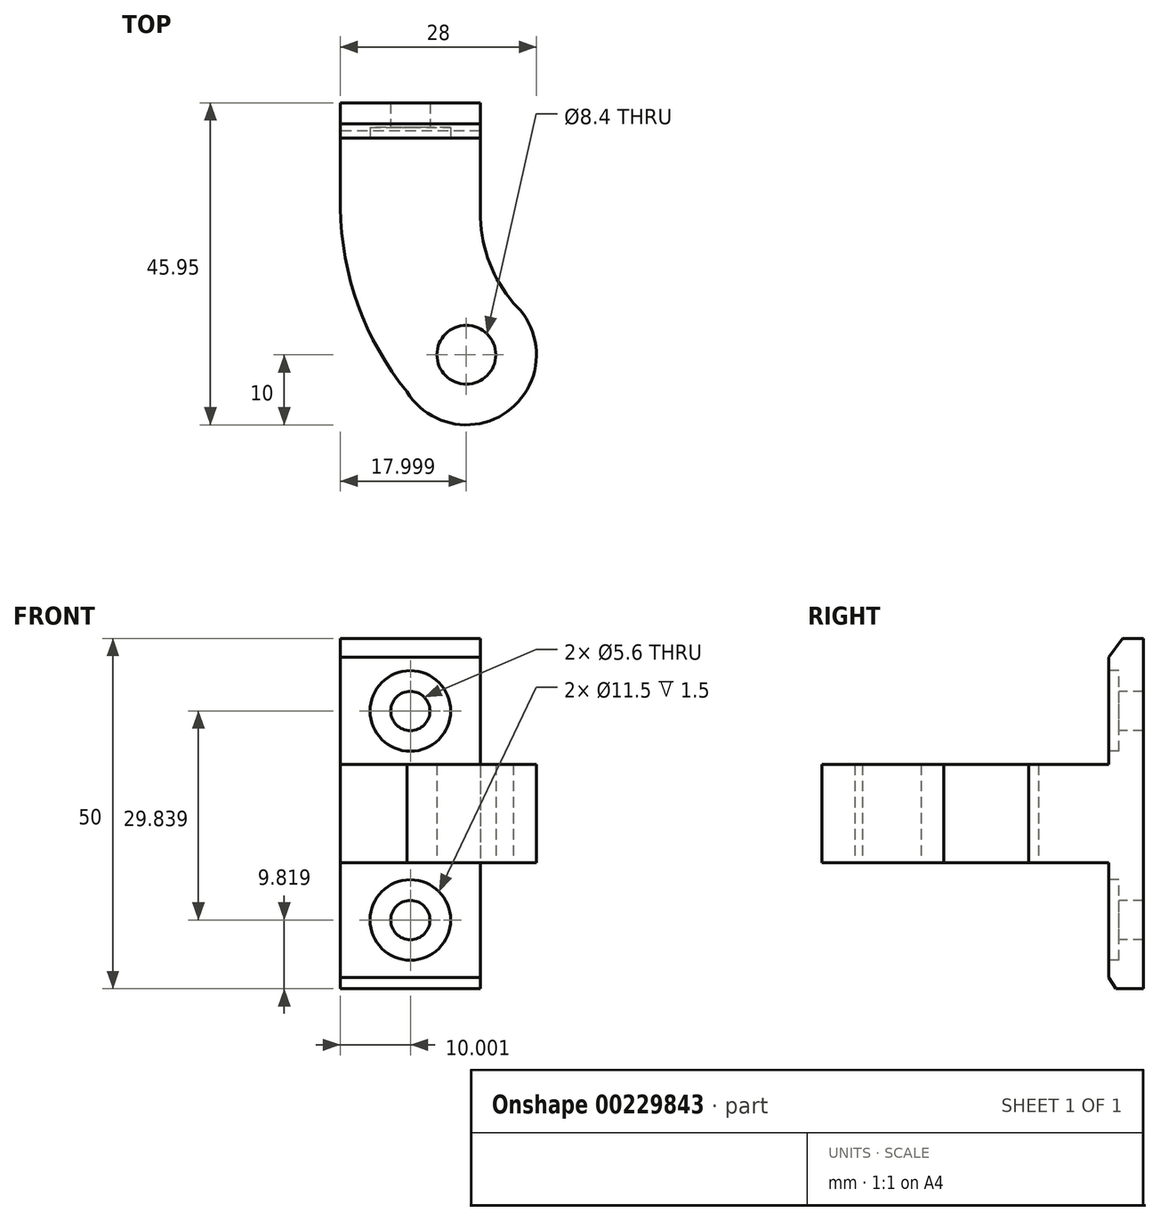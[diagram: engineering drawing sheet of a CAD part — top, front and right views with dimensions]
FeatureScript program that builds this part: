
annotation { "Feature Type Name" : "Feature", "Feature Type Description" : "" }
export const myFeature = defineFeature(function(context is Context, id is Id, definition is map)
    precondition{}
    {
        {
            var Q0;
            Q0=qCreatedBy(makeId("Top.planeOp"),FACE);
            var sketch = newSketch(context, id + "F0", { "sketchPlane" : qUnion([Q0])});
            skLineSegment(sketch, "E0.top", {"start": v(-27.88, 26.05) * mm, "end": v(-5.88, 26.05) * mm});
            skCircle(sketch, "E1", {"center": v(-7.88, -9.9) * mm, "radius": 4.2 * mm});
            skCircle(sketch, "E2", {"center": v(-15.88, 8.05) * mm, "radius": 2.75 * mm, "construction": true});
            skLineSegment(sketch, "E3.bottom", {"start": v(-25.88, 26.05) * mm, "end": v(-5.88, 26.05) * mm});
            skLineSegment(sketch, "E3.top", {"start": v(-19.99, -9.95) * mm, "end": v(-5.88, -9.95) * mm});
            skLineSegment(sketch, "E3.left", {"start": v(-25.88, 26.05) * mm, "end": v(-25.88, 11.06) * mm});
            skLineSegment(sketch, "E3.right", {"start": v(-5.88, 26.05) * mm, "end": v(-5.88, 9.64) * mm});
            skArc(sketch, "E4", {"start": v(-16.38, -15.17) * mm, "mid": v(-1.48, -17.58) * mm, "end": v(-1.16, -2.5) * mm});
            skArc(sketch, "E5", {"start": v(-25.88, 11.06) * mm, "mid": v(-23.32, -2.85) * mm, "end": v(-16.38, -15.17) * mm});
            skArc(sketch, "E6", {"start": v(-5.88, 11.06) * mm, "mid": v(-4.5, 3.04) * mm, "end": v(0, -3.74) * mm});
            skLineSegment(sketch, "E7.trimOffspring", {"start": v(-5.88, -6.2) * mm, "end": v(-5.88, -9.95) * mm});
            skPoint(sketch, "E8.orphan", {"position": v(-25.88, -9.95) * mm});
            skSolve(sketch);
        }
        {
            var Q0;
            Q0 = qSketchRegion(id + "F0", true);
            var Q1;
            {var subQ8=sQuery(id+"F0.wireOp",EDGE,"E3.bottom");Q1=makeQuery(id+"F0.imprint","IMPRINT",FACE,{"disambiguationData":[TD([[makeQuery(id+"F0.imprint","IMPRINT",EDGE,{"derivedFrom":subQ8}),-1.0]])]});}
            extrude(context, id + "F1", {"entities" : qUnion([Q0, Q1]), "depth" : 14 * mm});
        }
        {
            var Q0;
            Q0=makeQuery(id+"F1.opExtrude","CAP_FACE",FACE,{"disambiguationData":[OSD([sQuery(id+"F0.wireOp",EDGE,"E1"),sQuery(id+"F0.wireOp",EDGE,"E3.bottom"),sQuery(id+"F0.wireOp",EDGE,"E3.left"),sQuery(id+"F0.wireOp",EDGE,"E3.right"),sQuery(id+"F0.wireOp",EDGE,"E4"),sQuery(id+"F0.wireOp",EDGE,"E5"),sQuery(id+"F0.wireOp",EDGE,"E6")])],"isStart":false});
            var sketch = newSketch(context, id + "F2", { "sketchPlane" : qUnion([Q0])});
            skLineSegment(sketch, "E9.bottom", {"start": v(-25.88, 26.05) * mm, "end": v(-5.88, 26.05) * mm});
            skLineSegment(sketch, "E9.top", {"start": v(-25.88, 21.05) * mm, "end": v(-5.88, 21.05) * mm});
            skLineSegment(sketch, "E9.left", {"start": v(-25.88, 26.05) * mm, "end": v(-25.88, 21.05) * mm});
            skLineSegment(sketch, "E9.right", {"start": v(-5.88, 26.05) * mm, "end": v(-5.88, 21.05) * mm});
            skLineSegment(sketch, "E10", {"start": v(-25.88, 21.05) * mm, "end": v(-22.88, 21.05) * mm});
            skLineSegment(sketch, "E11", {"start": v(-5.88, 21.05) * mm, "end": v(-8.88, 21.05) * mm});
            skLineSegment(sketch, "E12", {"start": v(-8.88, 21.05) * mm, "end": v(-8.88, 1.78) * mm});
            skLineSegment(sketch, "E13", {"start": v(-22.88, 21.05) * mm, "end": v(-22.88, -4.02) * mm});
            skLineSegment(sketch, "E14", {"start": v(-5.88, 9.64) * mm, "end": v(-25.83, 9.64) * mm});
            skSolve(sketch);
        }
        {
            var Q0;
            Q0=makeQuery(id+"F2.imprint","IMPRINT",FACE,{"disambiguationData":[TD([[makeQuery(id+"F2.imprint","IMPRINT",EDGE,{"derivedFrom":sQuery(id+"F2.wireOp",EDGE,"E9.bottom")}),-1.0]])]});
            var Q1;
            {var subQ0=sQuery(id+"F2.wireOp",EDGE,"E10");Q1=makeQuery(id+"F2.imprint","IMPRINT",FACE,{"disambiguationData":[TD([[makeQuery(id+"F2.imprint","IMPRINT",EDGE,{"derivedFrom":subQ0}),-1.0]])]});}
            var Q2;
            {var subQ4=sQuery(id+"F2.wireOp",EDGE,"E11");Q2=makeQuery(id+"F2.imprint","IMPRINT",FACE,{"disambiguationData":[TD([[makeQuery(id+"F2.imprint","IMPRINT",EDGE,{"derivedFrom":subQ4}),1.0]])]});}
            extrude(context, id + "F3", {"entities" : qUnion([Q0, Q1, Q2]), "operationType" : NewBodyOperationType.ADD, "depth" : 18 * mm});
        }
        {
            var Q0;
            {var subQ0=sQuery(id+"F0.wireOp",EDGE,"E3.right");Q0=makeQuery(id+"F3.boolean.opBoolean","MERGE",FACE,{"derivedFrom":[makeQuery(id+"F1.opExtrude","SWEPT_FACE",FACE,{"disambiguationData":[OSD([subQ0])]}),makeQuery(id+"F3.opExtrude","SWEPT_FACE",FACE,{"disambiguationData":[OSD([subQ0,sQuery(id+"F2.wireOp",EDGE,"E9.right")])]})]});}
            var sketch = newSketch(context, id + "F4", { "sketchPlane" : qUnion([Q0])});
            skLineSegment(sketch, "E15", {"start": v(26.05, 32) * mm, "end": v(23.05, 32) * mm, "construction": true});
            skLineSegment(sketch, "E16", {"start": v(23.05, 32) * mm, "end": v(9.64, 14) * mm});
            skSolve(sketch);
        }
        {
            var Q0;
            {var subQ0=sQuery(id+"F4.wireOp",EDGE,"E16");Q0=makeQuery(id+"F4.imprint","IMPRINT",FACE,{"disambiguationData":[TD([[makeQuery(id+"F4.imprint","IMPRINT",EDGE,{"derivedFrom":subQ0}),-1.0]])]});}
            extrude(context, id + "F5", {"entities" : qUnion([Q0]), "operationType" : NewBodyOperationType.REMOVE, "oppositeDirection" : true, "depth" : 25 * mm});
        }
        {
            var Q0;
            Q0=makeQuery(id+"F3.opExtrude","SWEPT_FACE",FACE,{"disambiguationData":[OSD([sQuery(id+"F2.wireOp",EDGE,"E9.top")])]});
            var sketch = newSketch(context, id + "F6", { "sketchPlane" : qUnion([Q0])});
            skLineSegment(sketch, "E17", {"start": v(-22.88, 21.66) * mm, "end": v(-8.88, 21.66) * mm, "construction": true});
            skCircle(sketch, "E18", {"center": v(-15.88, 21.66) * mm, "radius": 2.8 * mm});
            skSolve(sketch);
        }
        {
            var Q0;
            Q0=makeQuery(id+"F6.imprint","IMPRINT",FACE,{"disambiguationData":[TD([[makeQuery(id+"F6.imprint","IMPRINT",EDGE,{"derivedFrom":sQuery(id+"F6.wireOp",EDGE,"E18")}),1.0]])]});
            extrude(context, id + "F7", {"entities" : qUnion([Q0]), "operationType" : NewBodyOperationType.REMOVE, "oppositeDirection" : true, "depth" : 25 * mm});
        }
        {
            var Q0;
            Q0=makeQuery(id+"F3.opExtrude","SWEPT_FACE",FACE,{"disambiguationData":[OSD([sQuery(id+"F2.wireOp",EDGE,"E9.top")])]});
            var sketch = newSketch(context, id + "F8", { "sketchPlane" : qUnion([Q0])});
            skLineSegment(sketch, "E19", {"start": v(-22.88, 21.66) * mm, "end": v(-8.88, 21.66) * mm, "construction": true});
            skCircle(sketch, "E20", {"center": v(-15.88, 21.66) * mm, "radius": 5.75 * mm});
            skSolve(sketch);
        }
        {
            var Q0;
            Q0=makeQuery(id+"F8.imprint","IMPRINT",FACE,{"disambiguationData":[TD([[makeQuery(id+"F8.imprint","IMPRINT",EDGE,{"derivedFrom":sQuery(id+"F8.wireOp",EDGE,"E20")}),1.0]])]});
            extrude(context, id + "F9", {"entities" : qUnion([Q0]), "operationType" : NewBodyOperationType.REMOVE, "oppositeDirection" : true, "depth" : 1.5 * mm});
        }
        {
            var Q0;
            Q0=makeQuery(id+"F1.opExtrude","CAP_FACE",FACE,{"disambiguationData":[OSD([sQuery(id+"F0.wireOp",EDGE,"E1"),sQuery(id+"F0.wireOp",EDGE,"E3.bottom"),sQuery(id+"F0.wireOp",EDGE,"E3.left"),sQuery(id+"F0.wireOp",EDGE,"E3.right"),sQuery(id+"F0.wireOp",EDGE,"E4"),sQuery(id+"F0.wireOp",EDGE,"E5"),sQuery(id+"F0.wireOp",EDGE,"E6")])],"isStart":true});
            var sketch = newSketch(context, id + "F10", { "sketchPlane" : qUnion([Q0])});
            skLineSegment(sketch, "E21.bottom", {"start": v(-25.88, -26.05) * mm, "end": v(-5.88, -26.05) * mm});
            skLineSegment(sketch, "E21.top", {"start": v(-25.88, -21.05) * mm, "end": v(-5.88, -21.05) * mm});
            skLineSegment(sketch, "E21.left", {"start": v(-25.88, -26.05) * mm, "end": v(-25.88, -21.05) * mm});
            skLineSegment(sketch, "E21.right", {"start": v(-5.88, -26.05) * mm, "end": v(-5.88, -21.05) * mm});
            skLineSegment(sketch, "E22", {"start": v(-25.88, -21.05) * mm, "end": v(-22.88, -21.05) * mm});
            skLineSegment(sketch, "E23", {"start": v(-22.88, -21.05) * mm, "end": v(-22.88, -11.06) * mm});
            skLineSegment(sketch, "E24", {"start": v(-22.88, -11.06) * mm, "end": v(-25.88, -11.06) * mm});
            skLineSegment(sketch, "E25", {"start": v(-5.88, -21.05) * mm, "end": v(-8.88, -21.05) * mm});
            skLineSegment(sketch, "E26", {"start": v(-8.88, -21.05) * mm, "end": v(-8.88, -11.06) * mm});
            skLineSegment(sketch, "E27", {"start": v(-8.88, -11.06) * mm, "end": v(-5.88, -11.06) * mm});
            skSolve(sketch);
        }
        {
            var Q0;
            {var subQ0=sQuery(id+"F10.wireOp",EDGE,"E22");Q0=makeQuery(id+"F10.imprint","IMPRINT",FACE,{"disambiguationData":[TD([[makeQuery(id+"F10.imprint","IMPRINT",EDGE,{"derivedFrom":subQ0}),1.0]])]});}
            var Q1;
            Q1=makeQuery(id+"F10.imprint","IMPRINT",FACE,{"disambiguationData":[TD([[makeQuery(id+"F10.imprint","IMPRINT",EDGE,{"derivedFrom":sQuery(id+"F10.wireOp",EDGE,"E21.bottom")}),1.0]])]});
            var Q2;
            {var subQ0=sQuery(id+"F10.wireOp",EDGE,"E25");Q2=makeQuery(id+"F10.imprint","IMPRINT",FACE,{"disambiguationData":[TD([[makeQuery(id+"F10.imprint","IMPRINT",EDGE,{"derivedFrom":subQ0}),-1.0]])]});}
            extrude(context, id + "F11", {"entities" : qUnion([Q0, Q1, Q2]), "operationType" : NewBodyOperationType.ADD, "depth" : 18 * mm});
        }
        {
            var Q0;
            {var subQ0=sQuery(id+"F0.wireOp",EDGE,"E3.left");Q0=makeQuery(id+"F11.boolean.opBoolean","MERGE",FACE,{"derivedFrom":[makeQuery(id+"F3.boolean.opBoolean","MERGE",FACE,{"derivedFrom":[makeQuery(id+"F1.opExtrude","SWEPT_FACE",FACE,{"disambiguationData":[OSD([subQ0])]}),makeQuery(id+"F3.opExtrude","SWEPT_FACE",FACE,{"disambiguationData":[OSD([subQ0,sQuery(id+"F2.wireOp",EDGE,"E9.left")])]})]}),makeQuery(id+"F11.opExtrude","SWEPT_FACE",FACE,{"disambiguationData":[OSD([subQ0,sQuery(id+"F10.wireOp",EDGE,"E21.left")])]})]});}
            var sketch = newSketch(context, id + "F12", { "sketchPlane" : qUnion([Q0])});
            skLineSegment(sketch, "E28", {"start": v(-26.05, -18) * mm, "end": v(-22.05, -18) * mm});
            skLineSegment(sketch, "E29", {"start": v(-22.05, -18) * mm, "end": v(-11.06, 0) * mm});
            skSolve(sketch);
        }
        {
            var Q0;
            Q0 = qSketchRegion(id + "F12", true);
            var Q1;
            {var subQ0=sQuery(id+"F12.wireOp",EDGE,"E29");Q1=makeQuery(id+"F12.imprint","IMPRINT",FACE,{"disambiguationData":[TD([[makeQuery(id+"F12.imprint","IMPRINT",EDGE,{"derivedFrom":subQ0}),-1.0]])]});}
            extrude(context, id + "F13", {"entities" : qUnion([Q0, Q1]), "operationType" : NewBodyOperationType.REMOVE, "oppositeDirection" : true, "depth" : 25 * mm});
        }
        {
            var Q0;
            Q0=makeQuery(id+"F11.opExtrude","SWEPT_FACE",FACE,{"disambiguationData":[OSD([sQuery(id+"F10.wireOp",EDGE,"E21.top")])]});
            var sketch = newSketch(context, id + "F14", { "sketchPlane" : qUnion([Q0])});
            skLineSegment(sketch, "E30", {"start": v(-22.88, -8.18) * mm, "end": v(-8.88, -8.18) * mm, "construction": true});
            skCircle(sketch, "E31", {"center": v(-15.88, -8.18) * mm, "radius": 2.8 * mm});
            skSolve(sketch);
        }
        {
            var Q0;
            Q0=makeQuery(id+"F14.imprint","IMPRINT",FACE,{"disambiguationData":[TD([[makeQuery(id+"F14.imprint","IMPRINT",EDGE,{"derivedFrom":sQuery(id+"F14.wireOp",EDGE,"E31")}),1.0]])]});
            extrude(context, id + "F15", {"entities" : qUnion([Q0]), "operationType" : NewBodyOperationType.REMOVE, "oppositeDirection" : true, "depth" : 25 * mm});
        }
        {
            var Q0;
            Q0=makeQuery(id+"F11.opExtrude","SWEPT_FACE",FACE,{"disambiguationData":[OSD([sQuery(id+"F10.wireOp",EDGE,"E21.top")])]});
            var sketch = newSketch(context, id + "F16", { "sketchPlane" : qUnion([Q0])});
            skLineSegment(sketch, "E32", {"start": v(-22.88, -8.18) * mm, "end": v(-8.88, -8.18) * mm, "construction": true});
            skCircle(sketch, "E33", {"center": v(-15.88, -8.18) * mm, "radius": 5.75 * mm});
            skSolve(sketch);
        }
        {
            var Q0;
            Q0=makeQuery(id+"F16.imprint","IMPRINT",FACE,{"disambiguationData":[TD([[makeQuery(id+"F16.imprint","IMPRINT",EDGE,{"derivedFrom":sQuery(id+"F16.wireOp",EDGE,"E33")}),1.0]])]});
            extrude(context, id + "F17", {"entities" : qUnion([Q0]), "operationType" : NewBodyOperationType.REMOVE, "oppositeDirection" : true, "depth" : 1.5 * mm});
        }
    });
